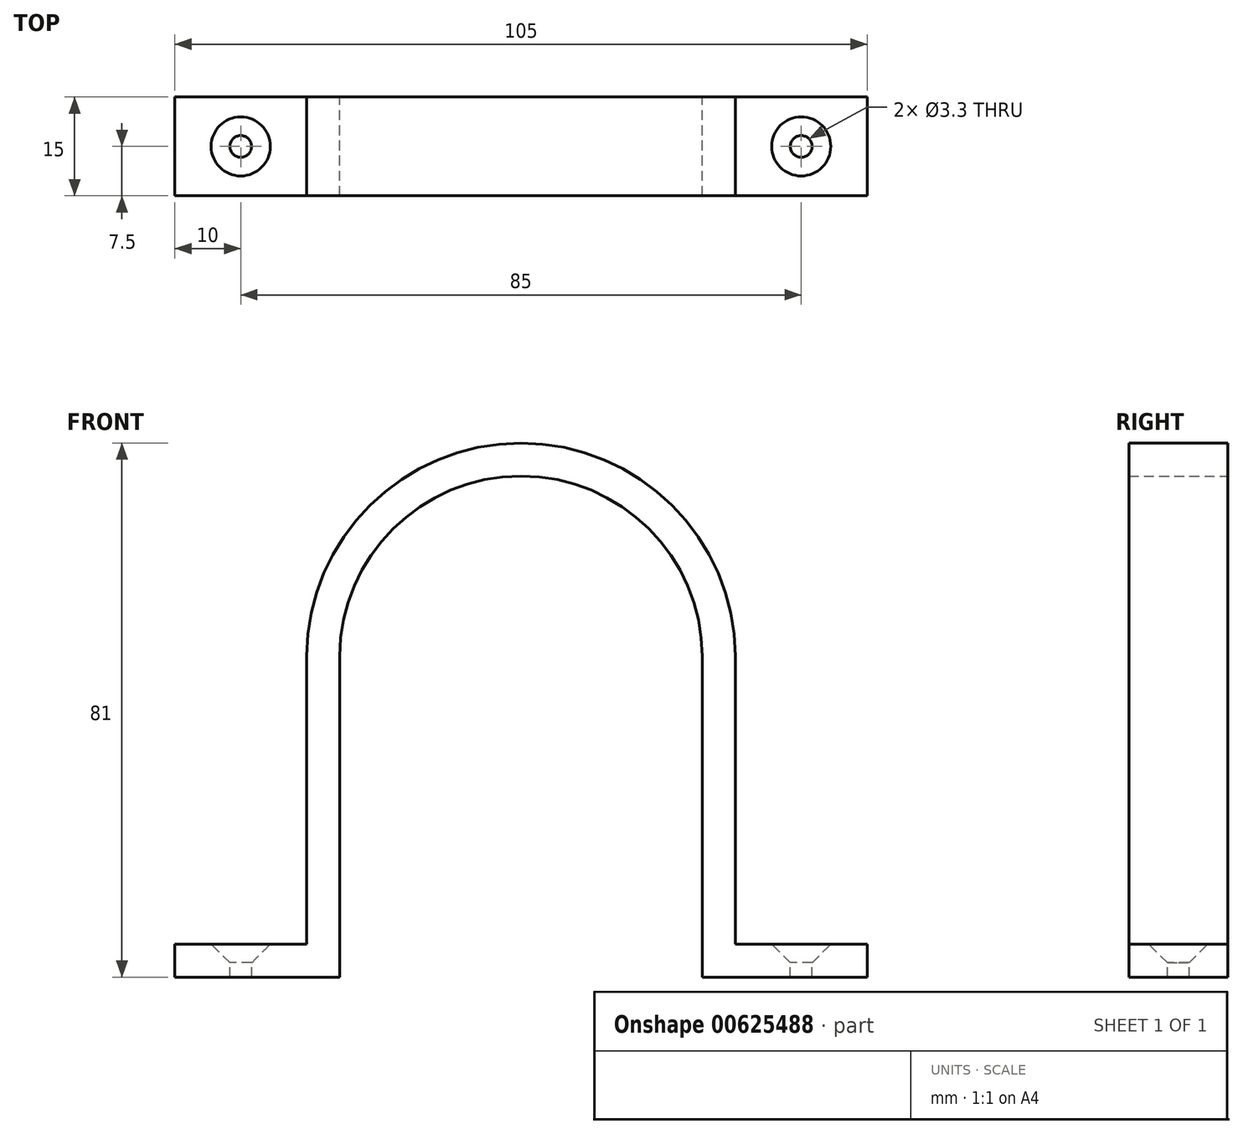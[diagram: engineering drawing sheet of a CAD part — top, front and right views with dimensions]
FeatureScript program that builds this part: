
annotation { "Feature Type Name" : "Feature", "Feature Type Description" : "" }
export const myFeature = defineFeature(function(context is Context, id is Id, definition is map)
    precondition{}
    {
        {
            assignVariable(context, id + "F0", {"name" : "thick", "anyValue" : 5});
        }
        {
            assignVariable(context, id + "F1", {"name" : "high", "anyValue" : 15});
        }
        {
            var Q0;
            Q0=qCreatedBy(makeId("Front.planeOp"),FACE);
            var sketch = newSketch(context, id + "F2", { "sketchPlane" : qUnion([Q0])});
            skLineSegment(sketch, "E0.bottom", {"start": v(32.5, 24.36) * mm, "end": v(-32.5, 24.36) * mm});
            skLineSegment(sketch, "E0.top", {"start": v(32.5, -24.36) * mm, "end": v(-32.5, -24.36) * mm});
            skLineSegment(sketch, "E0.left", {"start": v(32.5, 24.36) * mm, "end": v(32.5, -24.36) * mm});
            skLineSegment(sketch, "E0.right", {"start": v(-32.5, 24.36) * mm, "end": v(-32.5, -24.36) * mm});
            skPoint(sketch, "E0.middle", {"position": v(0, 0) * mm});
            skArc(sketch, "E1", {"start": v(32.5, 24.36) * mm, "mid": v(0, 56.64) * mm, "end": v(-32.5, 24.36) * mm});
            skSolve(sketch);
        }
        {
            var Q0;
            Q0=makeQuery(id+"F2.imprint","IMPRINT",FACE,{"disambiguationData":[TD([[makeQuery(id+"F2.imprint","IMPRINT",EDGE,{"derivedFrom":sQuery(id+"F2.wireOp",EDGE,"E0.bottom")}),1.0]])]});
            extrude(context, id + "F3", {"entities" : qUnion([Q0]), "depth" : (getVariable(context, 'high')) * mm, "offsetDistance" : 25 * mm});
        }
        {
            var Q0;
            Q0=makeQuery(id+"F2.imprint","IMPRINT",FACE,{"disambiguationData":[TD([[makeQuery(id+"F2.imprint","IMPRINT",EDGE,{"derivedFrom":sQuery(id+"F2.wireOp",EDGE,"E0.bottom")}),-1.0]])]});
            extrude(context, id + "F4", {"entities" : qUnion([Q0]), "operationType" : NewBodyOperationType.ADD, "depth" : (getVariable(context, 'high')) * mm, "offsetDistance" : 25 * mm});
        }
        {
            var Q0;
            Q0=qCreatedBy(makeId("Front.planeOp"),FACE);
            var sketch = newSketch(context, id + "F5", { "sketchPlane" : qUnion([Q0])});
            skLineSegment(sketch, "E2.bottom", {"start": v(-32.5, -24.36) * mm, "end": v(-52.5, -24.36) * mm});
            skLineSegment(sketch, "E2.top", {"start": v(-32.5, -19.36) * mm, "end": v(-52.5, -19.36) * mm});
            skLineSegment(sketch, "E2.left", {"start": v(-32.5, -24.36) * mm, "end": v(-32.5, -19.36) * mm});
            skLineSegment(sketch, "E2.right", {"start": v(-52.5, -24.36) * mm, "end": v(-52.5, -19.36) * mm});
            skLineSegment(sketch, "E3.bottom", {"start": v(32.5, -24.36) * mm, "end": v(52.5, -24.36) * mm});
            skLineSegment(sketch, "E3.top", {"start": v(32.5, -19.36) * mm, "end": v(52.5, -19.36) * mm});
            skLineSegment(sketch, "E3.left", {"start": v(32.5, -24.36) * mm, "end": v(32.5, -19.36) * mm});
            skLineSegment(sketch, "E3.right", {"start": v(52.5, -24.36) * mm, "end": v(52.5, -19.36) * mm});
            skSolve(sketch);
        }
        {
            var Q0;
            Q0=makeQuery(id+"F5.imprint","IMPRINT",FACE,{"disambiguationData":[TD([[makeQuery(id+"F5.imprint","IMPRINT",EDGE,{"derivedFrom":sQuery(id+"F5.wireOp",EDGE,"E2.bottom")}),-1.0]])]});
            var Q1;
            Q1=makeQuery(id+"F5.imprint","IMPRINT",FACE,{"disambiguationData":[TD([[makeQuery(id+"F5.imprint","IMPRINT",EDGE,{"derivedFrom":sQuery(id+"F5.wireOp",EDGE,"E3.bottom")}),1.0]])]});
            extrude(context, id + "F6", {"entities" : qUnion([Q0, Q1]), "operationType" : NewBodyOperationType.ADD, "depth" : (getVariable(context, 'high')) * mm, "offsetDistance" : 25 * mm});
        }
        {
            var Q0;
            {var subQ0=sQuery(id+"F2.wireOp",EDGE,"E0.bottom");Q0=makeQuery(id+"F6.boolean.opBoolean","MERGE",FACE,{"derivedFrom":[makeQuery(id+"F4.boolean.opBoolean","MERGE",FACE,{"derivedFrom":[makeQuery(id+"F3.opExtrude","CAP_FACE",FACE,{"disambiguationData":[OSD([subQ0,sQuery(id+"F2.wireOp",EDGE,"E0.top"),sQuery(id+"F2.wireOp",EDGE,"E0.left"),sQuery(id+"F2.wireOp",EDGE,"E0.right")])],"isStart":false}),makeQuery(id+"F4.opExtrude","CAP_FACE",FACE,{"disambiguationData":[OSD([subQ0,sQuery(id+"F2.wireOp",EDGE,"E1")])],"isStart":false})]}),makeQuery(id+"F6.opExtrude","CAP_FACE",FACE,{"disambiguationData":[OSD([sQuery(id+"F5.wireOp",EDGE,"E2.bottom"),sQuery(id+"F5.wireOp",EDGE,"E2.top"),sQuery(id+"F5.wireOp",EDGE,"E2.left"),sQuery(id+"F5.wireOp",EDGE,"E2.right")])],"isStart":false}),makeQuery(id+"F6.opExtrude","CAP_FACE",FACE,{"disambiguationData":[OSD([sQuery(id+"F5.wireOp",EDGE,"E3.bottom"),sQuery(id+"F5.wireOp",EDGE,"E3.top"),sQuery(id+"F5.wireOp",EDGE,"E3.left"),sQuery(id+"F5.wireOp",EDGE,"E3.right")])],"isStart":false})]});}
            var Q1;
            {var subQ0=sQuery(id+"F2.wireOp",EDGE,"E0.bottom");Q1=makeQuery(id+"F6.boolean.opBoolean","MERGE",FACE,{"derivedFrom":[makeQuery(id+"F4.boolean.opBoolean","MERGE",FACE,{"derivedFrom":[makeQuery(id+"F3.opExtrude","CAP_FACE",FACE,{"disambiguationData":[OSD([subQ0,sQuery(id+"F2.wireOp",EDGE,"E0.top"),sQuery(id+"F2.wireOp",EDGE,"E0.left"),sQuery(id+"F2.wireOp",EDGE,"E0.right")])],"isStart":true}),makeQuery(id+"F4.opExtrude","CAP_FACE",FACE,{"disambiguationData":[OSD([subQ0,sQuery(id+"F2.wireOp",EDGE,"E1")])],"isStart":true})]}),makeQuery(id+"F6.opExtrude","CAP_FACE",FACE,{"disambiguationData":[OSD([sQuery(id+"F5.wireOp",EDGE,"E2.bottom"),sQuery(id+"F5.wireOp",EDGE,"E2.top"),sQuery(id+"F5.wireOp",EDGE,"E2.left"),sQuery(id+"F5.wireOp",EDGE,"E2.right")])],"isStart":true}),makeQuery(id+"F6.opExtrude","CAP_FACE",FACE,{"disambiguationData":[OSD([sQuery(id+"F5.wireOp",EDGE,"E3.bottom"),sQuery(id+"F5.wireOp",EDGE,"E3.top"),sQuery(id+"F5.wireOp",EDGE,"E3.left"),sQuery(id+"F5.wireOp",EDGE,"E3.right")])],"isStart":true})]});}
            shell(context, id + "F7", {"entities" : qUnion([Q0, Q1]), "thickness" : (getVariable(context, 'thick')) * mm});
        }
        {
            var Q0;
            Q0=qCreatedBy(makeId("Front.planeOp"),FACE);
            var sketch = newSketch(context, id + "F8", { "sketchPlane" : qUnion([Q0])});
            skLineSegment(sketch, "E4.bottom", {"start": v(-27.5, -19.36) * mm, "end": v(27.5, -19.36) * mm});
            skLineSegment(sketch, "E4.top", {"start": v(-27.5, -25.61) * mm, "end": v(27.5, -25.61) * mm});
            skLineSegment(sketch, "E4.left", {"start": v(-27.5, -19.36) * mm, "end": v(-27.5, -25.61) * mm});
            skLineSegment(sketch, "E4.right", {"start": v(27.5, -19.36) * mm, "end": v(27.5, -25.61) * mm});
            skSolve(sketch);
        }
        {
            var Q0;
            Q0=makeQuery(id+"F8.imprint","IMPRINT",FACE,{"disambiguationData":[TD([[makeQuery(id+"F8.imprint","IMPRINT",EDGE,{"derivedFrom":sQuery(id+"F8.wireOp",EDGE,"E4.bottom")}),-1.0]])]});
            extrude(context, id + "F9", {"entities" : qUnion([Q0]), "operationType" : NewBodyOperationType.REMOVE, "oppositeDirection" : true, "depth" : (getVariable(context, 'high') * 2) * mm, "offsetDistance" : 25 * mm, "symmetric" : true});
        }
        {
            var Q0;
            Q0=makeQuery(id+"F6.opExtrude","SWEPT_FACE",FACE,{"disambiguationData":[OSD([sQuery(id+"F5.wireOp",EDGE,"E3.top")])]});
            var sketch = newSketch(context, id + "F10", { "sketchPlane" : qUnion([Q0])});
            skPoint(sketch, "E5", {"position": v(42.5, -7.5) * mm});
            skPoint(sketch, "E6", {"position": v(-42.5, -7.5) * mm});
            skSolve(sketch);
        }
        {
            var Q0;
            Q0=sQuery(id+"F10.wireOp",VERTEX,"E6");
            var Q1;
            Q1=sQuery(id+"F10.wireOp",VERTEX,"E5");
            var Q2;
            Q2=makeQuery(id+"F3.opExtrude","SWEPT_BODY",BODY,{"disambiguationData":[OSD([sQuery(id+"F2.wireOp",EDGE,"E0.bottom"),sQuery(id+"F2.wireOp",EDGE,"E0.top"),sQuery(id+"F2.wireOp",EDGE,"E0.left"),sQuery(id+"F2.wireOp",EDGE,"E0.right")])]});
            hole(context, id + "F11", {"style" : HoleStyle.C_SINK, "endStyle" : HoleEndStyle.BLIND, "standardTappedOrClearance" : lookupTablePath({ "standard" : "ISO", "engagement" : "75%", "pitch" : "0.7 mm", "size" : "M4", "type" : "Tapped" }), "standardBlindInLast" : lookupTablePath({ "standard" : "ISO", "engagement" : "75%", "pitch" : "0.7 mm", "size" : "M4", "type" : "Tapped" }), "holeDiameter" : 3.3 * mm, "cSinkDiameter" : 8.96 * mm, "cSinkAngle" : 90 * degree, "majorDiameter" : 4 * mm, "showTappedDepth" : true, "holeDepth" : (getVariable(context, 'thick') * 2) * mm, "isTappedThrough" : true, "tappedDepth" : 10 * mm, "tapClearance" : 0, "locations" : qUnion([Q0, Q1]), "scope" : qUnion([Q2])});
        }
    });
